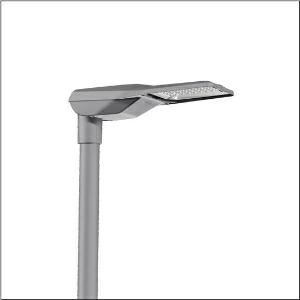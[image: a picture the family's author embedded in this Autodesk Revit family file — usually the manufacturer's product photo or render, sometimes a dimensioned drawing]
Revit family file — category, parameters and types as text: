
# Revit family: streetlight_sl_21_iq_mini___st0_5a_5xe2b31g08gb_b1a9
name_source: partatom
category: Lighting Fixtures
units: mm (PartAtom-declared; Revit-internal decimal feet)

## family parameters
Cut with Voids When Loaded = No
Host = Face
Light Source = No
Part Type = Normal
Room Calculation Point = No
Round Connector Dimension = Use Diameter
Shared = No

## types (1)
- --- (1 x LED, 5680 lm, 37.1 W, 3000K)
    Apparent Load = 37 VA
    CIE Flux Codes = 41 75 97 100 100
    Color Rendering = 70
    Color Temperature = 3000K
    Default Elevation = 1800 mm
    Description = Streetlight SL 21 iQ mini, mast luminaire, primary light control with lens, of PMMA, primary optical cover: cover, of toughened safety glass, transparent, light distribution: ST0.5a, light emission: direct distribution, primary light characteristic: asymmetric, installation type: post-top, side-entry, LED, High Power LED, rated luminous flux: 5.680lm, luminous efficacy: 153lm/W, light colour: 730, colour temperature: 3000K, control: Street-Remote, Auto-Match, Temp-Guard, Lumen-Switch, Night-Set, Smart-Wire, Light-Fading, Desk-Remote (wireless, voltage-free reading and setting of iQ features in the workshop via application-optimized NFC function/RFID function), optimised constant luminous flux control (CLO 2.0), presetting dimming linear, mains connection: 220..240V, AC, 50/60Hz, start of lifetime: 37W, end of service life: 39W, reduction: 18W, luminaire housing, of diecast aluminium, powder-coated, Siteco® metallic grey (DB 702S), corrosivity category C5 mid according to DIN EN ISO 12944, please order mast flange separately, inclination adjustable: 0°, 5°, 10°, 15°, sealing non-destructively replaceable, multi-level sealing system, length: 628mm, width: 235mm, height: 110mm, mast flange for spigot size: 42mm (side-entry): 5XC10008XM4, 60/48mm (side-entry/post-top): 5XC10108XM2, 76/60mm (side-entry/post-top): 5XC10108XM1, protection rating (complete): IP66, insulation class (complete): insulation class II (safety insulation), certification: CE, ENEC, ENEC+, VDE, impact resistance: IK09, permissible operating ambient temperature for outdoor applications: -40..+50°C, standard-compliant lighting for roads and squares, packaging unit: 1 piece

Light Distribution: ST0.5a
    Height = 110 mm
    Lamp = 1 x LED
    Lamp Light Flux = 5680 lm
    Lamp Power = 37.1 W
    Lamp count = 1
    Length = 625 mm
    Luminous efficacy = 153 lm/W
    Manufacturer = Siteco
    ModVariant = No
    Model = 5XE2B31G08GB
    Number of Poles = 1
    OnlyDefault = Yes
    Power Factor = 1
    Product Name = Streetlight SL 21 iQ mini | ST0.5a
    Product group = mast luminaire | pylon top
    ProductGroupID = 6100
    Protection Class = Protection class II
    Protection Degree = IP 66
    RLX_Detail_Level = 1
    RLX_Emergency_Light_Flux = 0 lm
    RLX_Emergency_Type = 0
    RLX_Emergency_Type_DB = No
    RlxData = <blob elided: 103537 chars, md5=4ec36d21>
    Socket = socket
    Standby Power = 0 W
    System Light Flux = 5680 lm
    System Power = 37 W
    Type Comments = factory setting: luminous flux: 100 % | dim-lin: 254 | 385 mA
    Type Image = l_1003519.jpg
    URL = http://relux.com
    VarID = @adj_125519
    Voltage = 0 V
    Weight = 0.00 kg
    Width = 234 mm

## geometry (parser evidence)
native form markers: Blend x4, Sweep x11
no freeform markers — native parametric forms only
